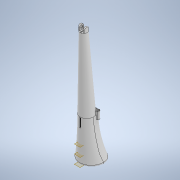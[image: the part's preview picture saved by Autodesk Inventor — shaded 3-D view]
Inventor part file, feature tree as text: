
AUTODESK INVENTOR PART (.ipt)
format: ipt  version: 2021 (Build 250183000, 183)  size: 871,936 bytes
history: native  units: mm
features: sketch x37, extrude x22, plane x17, fillet x4, hole x3, loft x2, revolve x2, other x1, thread x1
ambient origin geometry x8: Origin, YZ Plane, XZ Plane, XY Plane, X Axis, Y Axis, Z Axis, Center Point
bodies: Body1 (feature_tree)
feature tree (89):
  other  "Sólido1"
  plane  "Plano de trabajo1"
  plane  "Plano de trabajo2"
  plane  "Plano de trabajo4"
  plane  "Plano de trabajo5"
  plane  "Plano de trabajo6"
  sketch  "Boceto1"  dims[d1=250.0mm d2=0.0mm d3=-80.0mm d4=-110.0mm]
  sketch  "Boceto2"  dims[d5=-140.0mm d7=-0.0mm d8=2.0mm]
  sketch  "Boceto3"  dims[d9=140.0mm d10=250.0mm]
  sketch  "Boceto4"  dims[d11=24.0mm d22=0.0mm d23=90.0deg d24=0.0mm d25=90.0deg]
  sketch  "Boceto6"  dims[d44=45.0mm d49=29.11157mm]
  sketch  "Boceto7"  dims[d50=29.11157mm d53=29.11157mm]
  loft  "Solevación1"
  fillet  "Empalme2"  [1 undecoded]
  extrude  "Extrusión1"  TaperAngle=0.0deg  [1 undecoded]
  fillet  "Empalme5"  Radius=2.0mm
  plane  "Plano de trabajo7"
  extrude  "Extrusión2"  Depth=250.0mm
  plane  "Plano de trabajo8"
  plane  "Plano de trabajo9"
  loft  "Solevación9"
  plane  "Plano de trabajo10"
  extrude  "Extrusión3"  Depth=29.11157mm
  plane  "Plano de trabajo11"
  revolve  "Revolución1"  [1 undecoded]
  revolve  "Revolución2"  [1 undecoded]
  extrude  "Extrusión4"  Depth=32.5mm
  plane  "Plano de trabajo12"
  extrude  "Extrusión5"  Depth=44.747934mm
  plane  "Plano de trabajo13"
  plane  "Plano de trabajo14"
  extrude  "Extrusión6"  Depth=42.747934mm
  extrude  "Extrusión7"  Depth=42.747934mm
  extrude  "Extrusión8"  Depth=13.0mm
  extrude  "Extrusión11"  Depth=7.75mm
  extrude  "Extrusión9"  Depth=7.75mm
  extrude  "Extrusión10"  Depth=16.0mm
  extrude  "Extrusión12"  Depth=12.0mm
  sketch  "Boceto30"  dims[d160=-19.75mm d161=0.0mm]
  extrude  "Extrusión13"  Depth=7.75mm
  extrude  "Extrusión14"  Depth=7.75mm
  extrude  "Extrusión15"  TaperAngle=0.0deg  [1 undecoded]
  hole  "Agujero1"  [1 undecoded]
  thread  "Rosca1"  [1 undecoded]
  extrude  "Extrusión16"  Depth=2.0mm
  plane  "Plano de trabajo16"
  extrude  "Extrusión17"  TaperAngle=0.0deg  [1 undecoded]
  extrude  "Extrusión18"  TaperAngle=0.0deg  [1 undecoded]
  plane  "Plano de trabajo17"
  sketch  "Boceto46"  dims[d182=0.25mm]
  hole  "Agujero2"  [1 undecoded]
  hole  "Agujero3"  [1 undecoded]
  plane  "Plano de trabajo19"
  sketch  "Boceto50"  dims[d185=2.0mm]
  sketch  "Boceto45"  dims[d181=0.75mm]
  extrude  "Extrusión22"  Depth=12.0mm
  extrude  "Extrusión23"  [1 undecoded]
  extrude  "Extrusión24"  Depth=0.75mm
  plane  "Plano de trabajo20"
  extrude  "Extrusión25"  Depth=1.0mm
  fillet  "Empalme6"  Radius=11.0mm
  fillet  "Empalme7"  Radius=17.453293mm
  sketch  "Boceto44"  dims[d180=0.75mm]
  sketch  "Boceto47"  dims[d183=1.0mm]
  sketch  "Boceto49"  dims[d184=0.25mm]
  sketch  "Boceto9"  dims[d59=29.11157mm d61=29.11157mm]
  sketch  "Boceto10"  dims[d65=22.5mm d66=32.5mm]
  sketch  "Boceto15"  dims[d67=22.5mm d90=44.747934mm]
  sketch  "Boceto16"  dims[d91=42.747934mm d93=42.747934mm]
  sketch  "Boceto17"  dims[d96=0.0mm d97=90.0deg d98=0.0mm d99=90.0deg d100=0.0mm d101=90.0deg d102=0.0mm d103=90.0deg d112=42.747934mm]
  sketch  "Boceto18"  dims[d115=5.0mm d120=13.0mm]
  sketch  "Boceto19"  dims[d121=6.5mm d124=7.75mm]
  sketch  "Boceto20"  dims[d125=7.75mm d126=7.75mm]
  sketch  "Boceto21"  dims[d127=7.75mm d130=16.0mm]
  sketch  "Boceto22"  dims[d131=0.0mm d132=12.0mm]
  sketch  "Boceto24"  dims[d133=12.0mm d134=7.75mm]
  sketch  "Boceto25"  dims[d135=6.5mm d136=7.75mm]
  sketch  "Boceto26"  dims[d137=15.0mm d138=0.0mm]
  sketch  "Boceto27"  dims[d146=-8.5mm d147=30.0mm d148=2.0mm]
  sketch  "Boceto28"  dims[d149=25.12mm d150=2.0mm]
  sketch  "Boceto29"  dims[d151=10.357mm d156=0.0mm d157=90.0deg d158=0.0mm d159=90.0deg]
  sketch  "Boceto31"  dims[d163=0.0mm d164=2.0mm]
  sketch  "Boceto36"  dims[d165=15.0mm d166=4.0mm]
  sketch  "Boceto37"  dims[d167=30.0mm d168=12.0mm]
  sketch  "Boceto38"  dims[d169=0.0mm d170=-7.25mm]
  sketch  "Boceto39"  dims[d171=4.5mm d172=0.75mm]
  sketch  "Boceto40"  dims[d173=2.5mm d174=1.0mm d176=11.0mm d177=17.453293mm]
  sketch  "Boceto41"  dims[d179=2.939597mm]
  sketch  "Boceto51"  dims[d187=1.0mm d189=3.0mm d190=2.0mm d191=2.0mm d192=0.25mm d193=0.25mm d194=90.0deg d196=4.381635mm d197=0.0mm d198=-48.35mm d199=12.0mm d200=20.0mm d201=9.0mm d202=9.0mm d203=2.0mm d204=201.65mm d205=0.0mm d206=0.5mm d207=0.25mm d208=-7.5mm d209=100.0mm d210=0.0mm d211=35.0mm d212=0.0mm d213=210.0mm d214=0.0mm d215=2.0mm d216=1.059493mm d217=6.5mm d218=1.059493mm d219=5.0mm d220=2.0mm d221=0.0mm d222=2.0mm d223=6.5mm d224=1.059493mm d225=5.0mm d226=4.85mm d227=2.0mm d228=0.0mm d229=6.0mm d230=10.0mm d231=3.0mm d232=11.0mm d233=10.5mm d235=30.0deg d236=4.75mm d237=0.0mm d238=-17.0mm d239=100.0mm d240=0.0mm d241=6.5mm d242=1.65mm d243=3.3mm d244=15.6mm d245=2.0mm d247=16.0mm d248=2.0mm d249=0.0mm d250=4.5mm d251=0.75mm d252=2.5mm d253=1.0mm d254=11.0mm d255=17.453293mm d256=2.939597mm d257=0.75mm d258=0.75mm d259=0.25mm d260=1.0mm d261=0.25mm d262=2.0mm d263=1.0mm d264=3.0mm d265=2.0mm d266=2.0mm d267=0.25mm d268=0.25mm d269=40.0mm d270=1.0mm d271=1.0mm d272=7.75mm d273=0.5mm d274=8.5mm d275=90.0deg d276=0.0mm d277=17.75mm d280=22.5mm d281=2.0mm d282=0.0mm d283=0.0mm d292=2.0mm d293=0.0mm d296=3.5mm d297=0.0mm d299=4.0mm d300=3.708mm d301=3.023mm d302=2.0mm d303=14.3117mm d304=16.0mm d305=0.0mm d306=16.0mm d307=0.0mm d314=6.0mm d315=19.2mm d316=6.0mm d317=19.2mm d318=13.0mm d320=6.0mm d321=19.2mm d322=13.0mm d323=6.0mm d324=19.2mm d325=13.0mm d326=7.0mm d332=10.0mm d333=0.0mm d335=-41.6mm d336=4.0mm d337=1.0mm d338=9.0mm d339=4.0mm d340=1.0mm d341=9.0mm d342=4.0mm d343=5.2mm d344=6.0mm d345=0.0mm d346=15.0mm d347=5.0mm d349=5.0mm d351=0.0mm d352=45.0mm d354=10.0mm d355=10.0mm d356=0.0mm d357=15.0mm d358=0.0mm d359=2.0mm d363=50.4125mm d376=14.059493mm d377=2.0mm d378=0.0mm d379=2.0mm d380=11.25mm d381=90.0mm d382=290.0mm d383=14.059493mm d384=100.825mm d390=30.940507mm d391=2.0mm d392=100.825mm d393=14.790546mm d394=2.0mm d395=3.0mm d396=6.0mm d397=4.0mm d398=4.0mm d399=4.0mm d400=8.128453mm d401=12.0mm d402=4.45mm d403=2.5mm d404=1.65mm d405=1.65mm d406=1.0mm d407=2.0mm d408=2.0mm d409=0.0mm d411=50.4125mm d412=6.0mm d418=13.059493mm d419=6.5mm d420=6.5mm d421=50.4125mm d422=126.03125mm d423=0.0mm d424=15.0mm d425=5.0mm d426=5.0mm d427=0.0mm d428=45.0mm d429=10.0mm d430=2.0mm d431=4.0mm d432=6.0mm d433=8.0mm d434=2.0mm d435=90.0deg d436=20.0mm d437=0.0mm d438=4.0mm d439=6.0mm d440=8.0mm d441=2.0mm d442=90.0deg d443=20.0mm d444=0.0mm d446=10.0mm d447=3.0mm d448=11.5mm d450=9.0mm d451=9.0mm d452=90.0mm d453=750.0mm d454=22.5mm d455=43.0mm d456=44.0mm d457=14.059493mm d458=11.25mm d461=22.5mm d462=43.0mm d463=7.059493mm d464=3.0mm d465=6.0mm d466=3.0mm d467=6.0mm d468=45.0mm d469=130.0mm d470=17.04mm d471=30.0mm d472=15.0mm d473=1.5mm d474=1.5mm d475=2.0mm d476=1.5mm d477=2.0mm d478=120.0mm d479=0.0mm d480=120.0mm d481=0.0mm d482=116.0mm d483=0.0mm d484=69.0mm d485=0.0mm d486=-3.0mm d487=65.395511mm d488=2.6mm d489=60.0deg d490=45.0deg d491=15.0mm d492=1.6mm d493=0.0mm]
note: 12 required parameter values undecoded (feature->parameter linkage not recoverable at this tier; creation-order binding heuristic only, values carry confidence <= 0.55)